# Revit family: Deca_Cuba redonda de apoio gota_Circolo_L.12050.GT
name_source: partatom
category: Plumbing Fixtures
units: mm (PartAtom-declared; Revit-internal decimal feet)

## family parameters
Cut with Voids When Loaded = No
Host = Face
Part Type = Normal
Room Calculation Point = No
Round Connector Dimension = Use Radius
Shared = No

## types (1)
- L.12050.GT.16_Branco Fosco
    Acompanha o Produto = Folheto 7920266
    Aprovado por = quattroD
    Atendimento ao Cliente = 0800-0117073
    Categoria = Cubas
    Composição Anel Vedação = -
    Composição Assento = -
    Composição Básica = Argila; feldspato; caulim; vidrados e corantes inorgânicos.
    Composição Componente = Aço inoxidável; elastômeros e plásticos de engenharia.
    Consumo = -
    Cor Interna = 16 - Branco Fosco
    Cor Principal = 16 - Branco Fosco
    Cor Secundária = -
    Cores Componente = -
    Criado por = quattroD
    Código Pai = L.12050.GT
    Default Elevation = 0 mm  [stored 0 ft]
    Description = CUBA REDONDA DE APOIO GOTA 50 CM - BRANCO FOSCO
    Diâmetro Ponto de Esgoto = 25 mm  [stored 0.082021 ft]
    Informações Complementares = -
    Itens de Instalação = -
    Linha = Circolo
    Manufacturer = Deca
    Material = Deca_Branco Fosco
    Model = L.12050.GT.16
    Norma = NBR-16728-1;NBR-16728-2
    Peso Líquido (Kg) = 8352
    Pressão máx. funcionamento = -
    Pressão mín. Aquec. Acúmulo = -
    Pressão mín. Aquec. Passagem = -
    Pressão mín. funcionamento = -
    Raio Ponto de Esgoto = 13 mm  [stored 0.0426509 ft]
    Saída de Esgoto = Válvula Curta
    Segmento = Banheiro Luxo
    Tipo de dispositivo economizador = -
    Tipo de mecanismo utilizado = -
    Tipo de rosca de entrada = -
    Tipo de rosca de saída = -
    URL = www.deca.com.br
    Vazão na Pressão máx. (L/min) = -
    Vazão na Pressão mín. (L/min) = -

note: [stored X ft] marks values corroborated as IEEE doubles in the binary element streams (Revit-internal decimal feet)

## geometry (parser evidence)
native form markers: Sweep x3
no freeform markers — native parametric forms only
